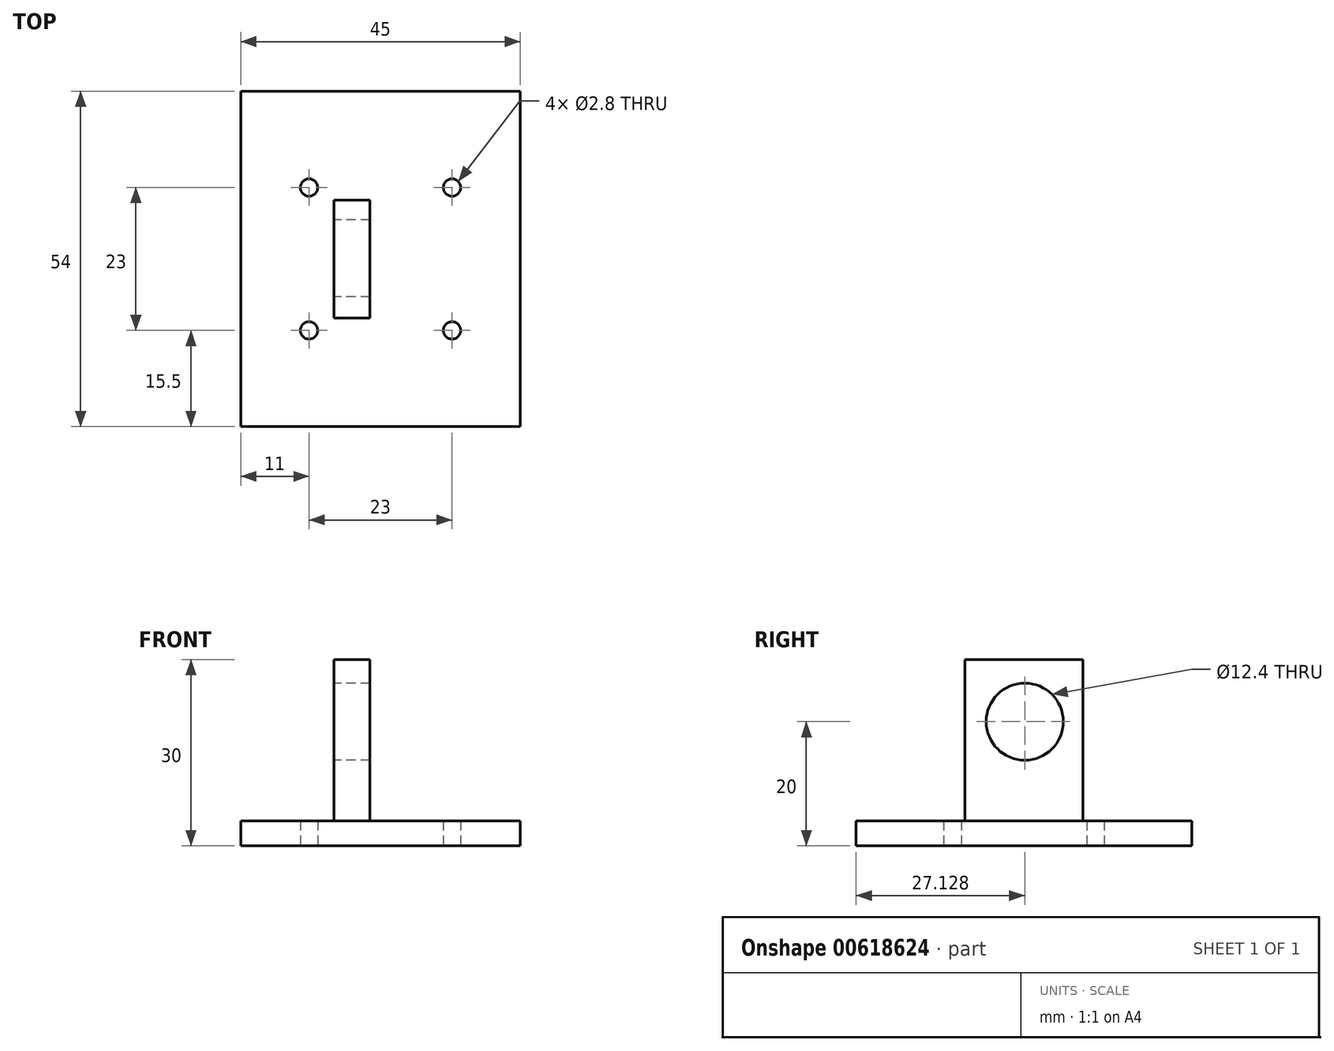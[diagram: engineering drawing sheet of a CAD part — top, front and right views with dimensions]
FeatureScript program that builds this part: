
annotation { "Feature Type Name" : "Feature", "Feature Type Description" : "" }
export const myFeature = defineFeature(function(context is Context, id is Id, definition is map)
    precondition{}
    {
        {
            var Q0;
            Q0=qCreatedBy(makeId("Top.planeOp"),FACE);
            var sketch = newSketch(context, id + "F0", { "sketchPlane" : qUnion([Q0])});
            skPoint(sketch, "E0.0", {"position": v(0, 0) * mm});
            skPoint(sketch, "E0.1", {"position": v(45, 0) * mm});
            skCircle(sketch, "E1.0", {"center": v(11, 38.5) * mm, "radius": 1.4 * mm});
            skCircle(sketch, "E1.1", {"center": v(34, 38.5) * mm, "radius": 1.4 * mm});
            skCircle(sketch, "E1.2", {"center": v(34, 15.5) * mm, "radius": 1.4 * mm});
            skCircle(sketch, "E1.3", {"center": v(11, 15.5) * mm, "radius": 1.4 * mm});
            skLineSegment(sketch, "E1.4", {"start": v(45, 54) * mm, "end": v(0, 54) * mm});
            skLineSegment(sketch, "E2", {"start": v(0, 54) * mm, "end": v(0, 0) * mm});
            skLineSegment(sketch, "E3", {"start": v(0, 0) * mm, "end": v(45, 0) * mm});
            skLineSegment(sketch, "E4", {"start": v(45, 54) * mm, "end": v(45, 0) * mm});
            skLineSegment(sketch, "E5.0", {"start": v(15, 36.5) * mm, "end": v(15, 17.5) * mm});
            skLineSegment(sketch, "E5.1", {"start": v(20.8, 36.5) * mm, "end": v(20.8, 17.5) * mm});
            skLineSegment(sketch, "E6", {"start": v(15, 17.5) * mm, "end": v(20.8, 17.5) * mm});
            skLineSegment(sketch, "E7", {"start": v(15, 36.5) * mm, "end": v(20.8, 36.5) * mm});
            skSolve(sketch);
        }
        {
            var Q0;
            Q0=makeQuery(id+"F0.imprint","IMPRINT",FACE,{"disambiguationData":[TD([[makeQuery(id+"F0.imprint","IMPRINT",EDGE,{"derivedFrom":sQuery(id+"F0.wireOp",EDGE,"E1.0")}),-1.0]])]});
            extrude(context, id + "F1", {"entities" : qUnion([Q0]), "depth" : 4 * mm, "offsetDistance" : 25 * mm});
        }
        {
            var Q0;
            Q0=makeQuery(id+"F0.imprint","IMPRINT",FACE,{"disambiguationData":[TD([[makeQuery(id+"F0.imprint","IMPRINT",EDGE,{"derivedFrom":sQuery(id+"F0.wireOp",EDGE,"E5.0")}),1.0]])]});
            extrude(context, id + "F2", {"entities" : qUnion([Q0]), "operationType" : NewBodyOperationType.ADD, "depth" : 30 * mm, "offsetDistance" : 25 * mm});
        }
        {
            var Q0;
            Q0=qCreatedBy(makeId("Right.planeOp"),FACE);
            var sketch = newSketch(context, id + "F3", { "sketchPlane" : qUnion([Q0])});
            skCircle(sketch, "E8.0", {"center": v(27.13, 20) * mm, "radius": 6.2 * mm});
            skLineSegment(sketch, "E9.0", {"start": v(36.5, 30) * mm, "end": v(36.5, 4) * mm});
            skLineSegment(sketch, "E9.1", {"start": v(17.5, 30) * mm, "end": v(17.5, 4) * mm});
            skLineSegment(sketch, "E9.2", {"start": v(36.5, 30) * mm, "end": v(17.5, 30) * mm});
            skSolve(sketch);
        }
        {
            var Q0;
            Q0 = qSketchRegion(id + "F3", true);
            extrude(context, id + "F4", {"entities" : qUnion([Q0]), "operationType" : NewBodyOperationType.REMOVE, "depth" : 25 * mm, "offsetDistance" : 25 * mm});
        }
    });
